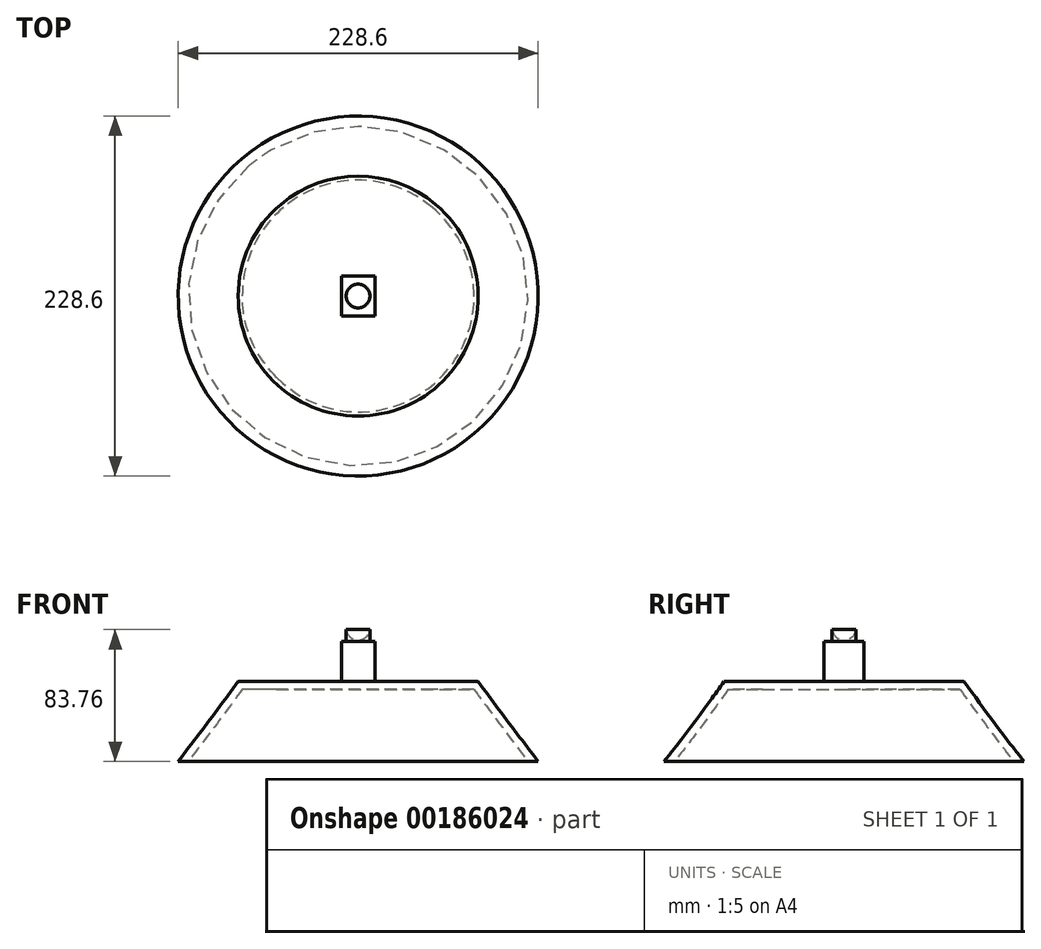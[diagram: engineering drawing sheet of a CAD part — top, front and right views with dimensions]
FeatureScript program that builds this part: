
annotation { "Feature Type Name" : "Feature", "Feature Type Description" : "" }
export const myFeature = defineFeature(function(context is Context, id is Id, definition is map)
    precondition{}
    {
        {
            var Q0;
            Q0=qCreatedBy(makeId("Top.planeOp"),FACE);
            var sketch = newSketch(context, id + "F0", { "sketchPlane" : qUnion([Q0])});
            skCircle(sketch, "E0", {"center": v(0, 0) * mm, "radius": 114.3 * mm});
            skSolve(sketch);
        }
        {
            var Q0;
            Q0=makeQuery(id+"F0.imprint","IMPRINT",FACE,{"disambiguationData":[TD([[makeQuery(id+"F0.imprint","IMPRINT",EDGE,{"derivedFrom":sQuery(id+"F0.wireOp",EDGE,"E0")}),1.0]])]});
            cPlane(context, id + "F1", {"entities" : qUnion([Q0]), "cplaneType" : CPlaneType.OFFSET, "offset" : 50.8 * mm, "width" : 152.4 * mm, "height" : 152.4 * mm});
        }
        {
            var Q0;
            Q0=qCreatedBy(id+"F1.planeOp",FACE);
            var sketch = newSketch(context, id + "F2", { "sketchPlane" : qUnion([Q0])});
            skArc(sketch, "E1", {"start": v(-49.1, 58.27) * mm, "mid": v(-69.1, 32.13) * mm, "end": v(-76.2, 0) * mm});
            skArc(sketch, "E2", {"start": v(49.1, 58.27) * mm, "mid": v(0, 76.2) * mm, "end": v(-49.1, 58.27) * mm});
            skArc(sketch, "E3", {"start": v(53.94, -53.82) * mm, "mid": v(70.42, -29.12) * mm, "end": v(76.2, 0) * mm});
            skArc(sketch, "E4", {"start": v(-53.94, -53.82) * mm, "mid": v(0, -76.2) * mm, "end": v(53.94, -53.82) * mm});
            skArc(sketch, "E5", {"start": v(-76.2, 0) * mm, "mid": v(-70.42, -29.12) * mm, "end": v(-53.94, -53.82) * mm});
            skArc(sketch, "E6", {"start": v(76.2, 0) * mm, "mid": v(69.1, 32.13) * mm, "end": v(49.1, 58.27) * mm});
            skSolve(sketch);
        }
        {
            var Q0;
            Q0 = qSketchRegion(id + "F0", true);
            var Q1;
            Q1 = qSketchRegion(id + "F2", true);
            loft(context, id + "F3", {"sheetProfilesArray" : [{ "sheetProfileEntities" : qUnion([Q0]) }, { "sheetProfileEntities" : qUnion([Q1]) }]});
        }
        {
            var Q0;
            Q0=makeQuery(id+"F3.opLoft","CAP_FACE",FACE,{"disambiguationData":[OSD([makeQuery(id+"F0.imprint","IMPRINT",FACE,{"disambiguationData":[TD([[makeQuery(id+"F0.imprint","IMPRINT",EDGE,{"derivedFrom":sQuery(id+"F0.wireOp",EDGE,"E0")}),1.0]])]})])],"isStart":true});
            shell(context, id + "F4", {"entities" : qUnion([Q0]), "thickness" : 5.08 * mm});
        }
        {
            var Q0;
            Q0=makeQuery(id+"F3.opLoft","CAP_FACE",FACE,{"disambiguationData":[OSD([makeQuery(id+"F2.imprint","IMPRINT",FACE,{"disambiguationData":[TD([[makeQuery(id+"F2.imprint","IMPRINT",EDGE,{"derivedFrom":sQuery(id+"F2.wireOp",EDGE,"E1")}),1.0]])]})])],"isStart":true});
            var sketch = newSketch(context, id + "F5", { "sketchPlane" : qUnion([Q0])});
            skLineSegment(sketch, "E7.bottom", {"start": v(10.64, 12.74) * mm, "end": v(-10.64, 12.74) * mm});
            skLineSegment(sketch, "E7.top", {"start": v(10.64, -12.74) * mm, "end": v(-10.64, -12.74) * mm});
            skLineSegment(sketch, "E7.left", {"start": v(10.64, 12.74) * mm, "end": v(10.64, -12.74) * mm});
            skLineSegment(sketch, "E7.right", {"start": v(-10.64, 12.74) * mm, "end": v(-10.64, -12.74) * mm});
            skPoint(sketch, "E7.middle", {"position": v(0, 0) * mm});
            skSolve(sketch);
        }
        {
            var Q0;
            Q0 = qSketchRegion(id + "F5", true);
            extrude(context, id + "F6", {"entities" : qUnion([Q0]), "operationType" : NewBodyOperationType.ADD, "depth" : 25.4 * mm, "offsetDistance" : 25.4 * mm});
        }
        {
            var Q0;
            Q0=makeQuery(id+"F6.opExtrude","SWEPT_FACE",FACE,{"disambiguationData":[OSD([sQuery(id+"F5.wireOp",EDGE,"E7.left")])]});
            cPlane(context, id + "F7", {"entities" : qUnion([Q0]), "cplaneType" : CPlaneType.OFFSET, "offset" : 10.7 * mm, "oppositeDirection" : true, "width" : 152.4 * mm, "height" : 152.4 * mm});
        }
        {
            var Q0;
            Q0=qCreatedBy(id+"F7.planeOp",FACE);
            var sketch = newSketch(context, id + "F8", { "sketchPlane" : qUnion([Q0])});
            skLineSegment(sketch, "E8", {"start": v(7.55, 76.17) * mm, "end": v(7.55, 83.76) * mm});
            skArc(sketch, "E9", {"start": v(0, 76.88) * mm, "mid": v(5.02, 78.95) * mm, "end": v(7.55, 83.76) * mm});
            skLineSegment(sketch, "E10", {"start": v(0, 76.88) * mm, "end": v(0, 76.17) * mm});
            skLineSegment(sketch, "E11", {"start": v(0, 76.17) * mm, "end": v(7.55, 76.17) * mm});
            skLineSegment(sketch, "E12", {"start": v(0, 75.72) * mm, "end": v(0, 79.66) * mm});
            skSolve(sketch);
        }
        {
            var Q0;
            Q0 = qSketchRegion(id + "F8", true);
            var Q1;
            Q1=sQuery(id+"F8.wireOp",EDGE,"E12");
            revolve(context, id + "F9", {"operationType" : NewBodyOperationType.ADD, "entities" : qUnion([Q0]), "axis" : qUnion([Q1]), "revolveType" : RevolveType.FULL});
        }
    });
